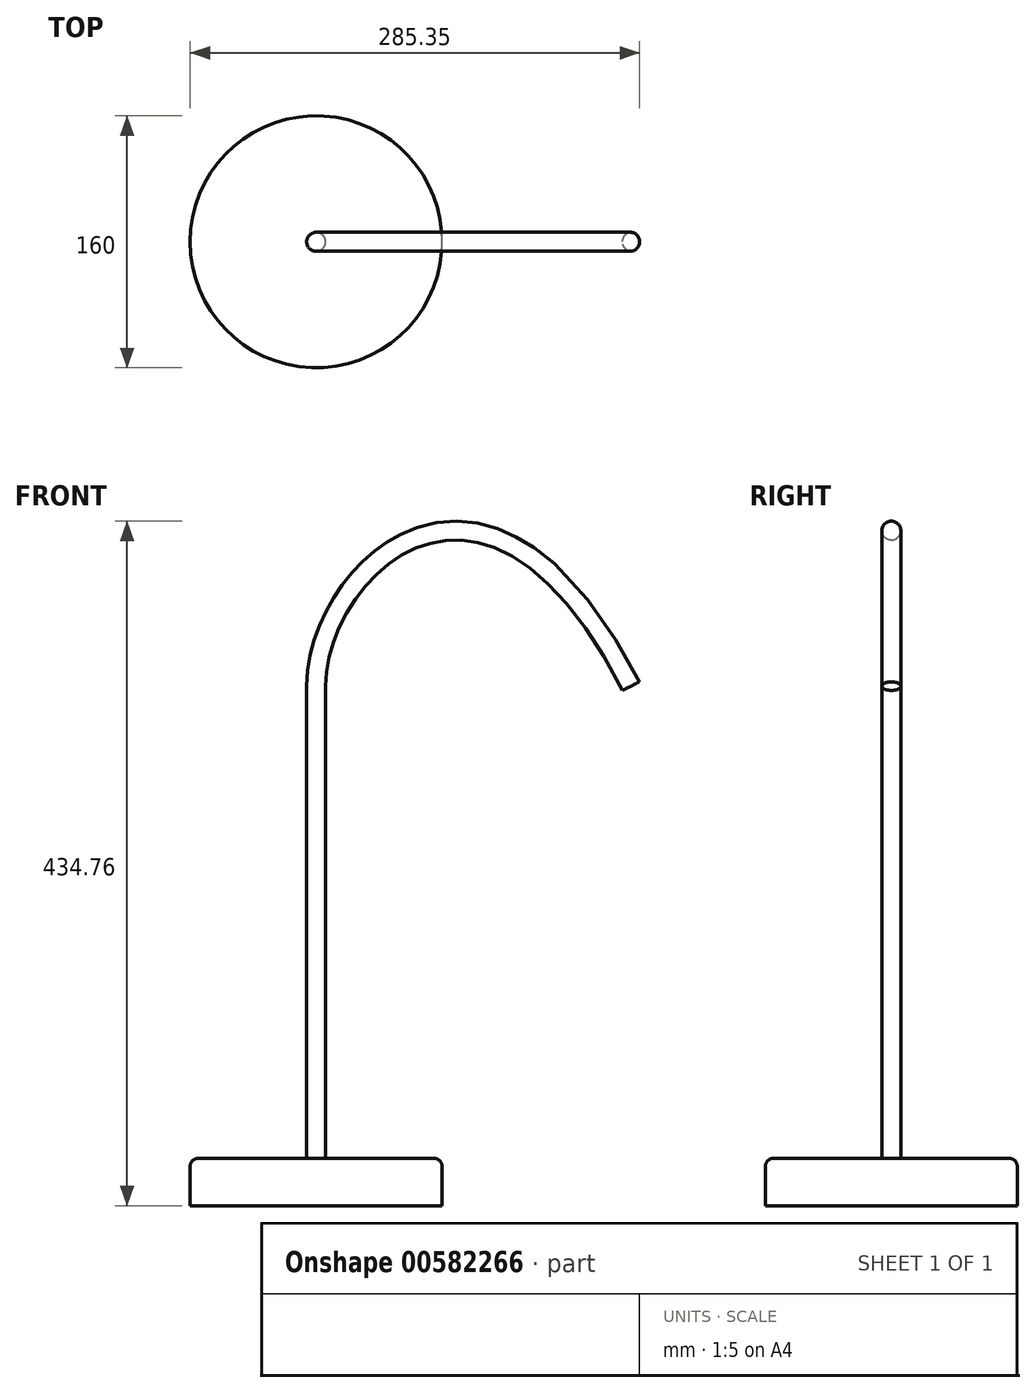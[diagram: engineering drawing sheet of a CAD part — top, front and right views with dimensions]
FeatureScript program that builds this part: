
annotation { "Feature Type Name" : "Feature", "Feature Type Description" : "" }
export const myFeature = defineFeature(function(context is Context, id is Id, definition is map)
    precondition{}
    {
        {
            var Q0;
            Q0=qCreatedBy(makeId("Top.planeOp"),FACE);
            var sketch = newSketch(context, id + "F0", { "sketchPlane" : qUnion([Q0])});
            skCircle(sketch, "E0", {"center": v(0, 0) * mm, "radius": 80 * mm});
            skSolve(sketch);
        }
        {
            var Q0;
            Q0=makeQuery(id+"F0.imprint","IMPRINT",FACE,{"disambiguationData":[TD([[makeQuery(id+"F0.imprint","IMPRINT",EDGE,{"derivedFrom":sQuery(id+"F0.wireOp",EDGE,"E0")}),1.0]])]});
            extrude(context, id + "F1", {"entities" : qUnion([Q0]), "oppositeDirection" : true, "depth" : 30 * mm, "offsetDistance" : 25 * mm});
        }
        {
            var Q0;
            Q0=makeQuery(id+"F1.opExtrude","CAP_EDGE",EDGE,{"disambiguationData":[OSD([sQuery(id+"F0.wireOp",EDGE,"E0")])],"isStart":true});
            fillet(context, id + "F2", {"entities" : qUnion([Q0]), "radius" : 5 * mm, "tangentPropagation" : true, "allowEdgeOverflow" : false});
        }
        {
            var Q0;
            Q0=qCreatedBy(makeId("Front.planeOp"),FACE);
            var sketch = newSketch(context, id + "F3", { "sketchPlane" : qUnion([Q0])});
            skLineSegment(sketch, "E1", {"start": v(0, 0) * mm, "end": v(0, 300) * mm});
            skFitSpline(sketch, "E2", {"points": [v(0, 300) * mm, v(200, 300) * mm], "startDerivative": vector(0, 222.56) * mm, "endDerivative": vector(273.2, -537.3) * mm});
            skSolve(sketch);
        }
        {
            var Q0;
            Q0=qCreatedBy(makeId("Top.planeOp"),FACE);
            var sketch = newSketch(context, id + "F4", { "sketchPlane" : qUnion([Q0])});
            skCircle(sketch, "E3", {"center": v(0, 0) * mm, "radius": 6 * mm});
            skSolve(sketch);
        }
        {
            var Q0;
            Q0=makeQuery(id+"F4.imprint","IMPRINT",FACE,{"disambiguationData":[TD([[makeQuery(id+"F4.imprint","IMPRINT",EDGE,{"derivedFrom":sQuery(id+"F4.wireOp",EDGE,"E3")}),1.0]])]});
            var Q1;
            Q1 = qConstructionFilter(qBodyType(qCreatedBy(id + "F3" ,EDGE), BodyType.WIRE), ConstructionObject.NO);
            sweep(context, id + "F5", {"profiles" : qUnion([Q0]), "path" : qUnion([Q1])});
        }
    });
